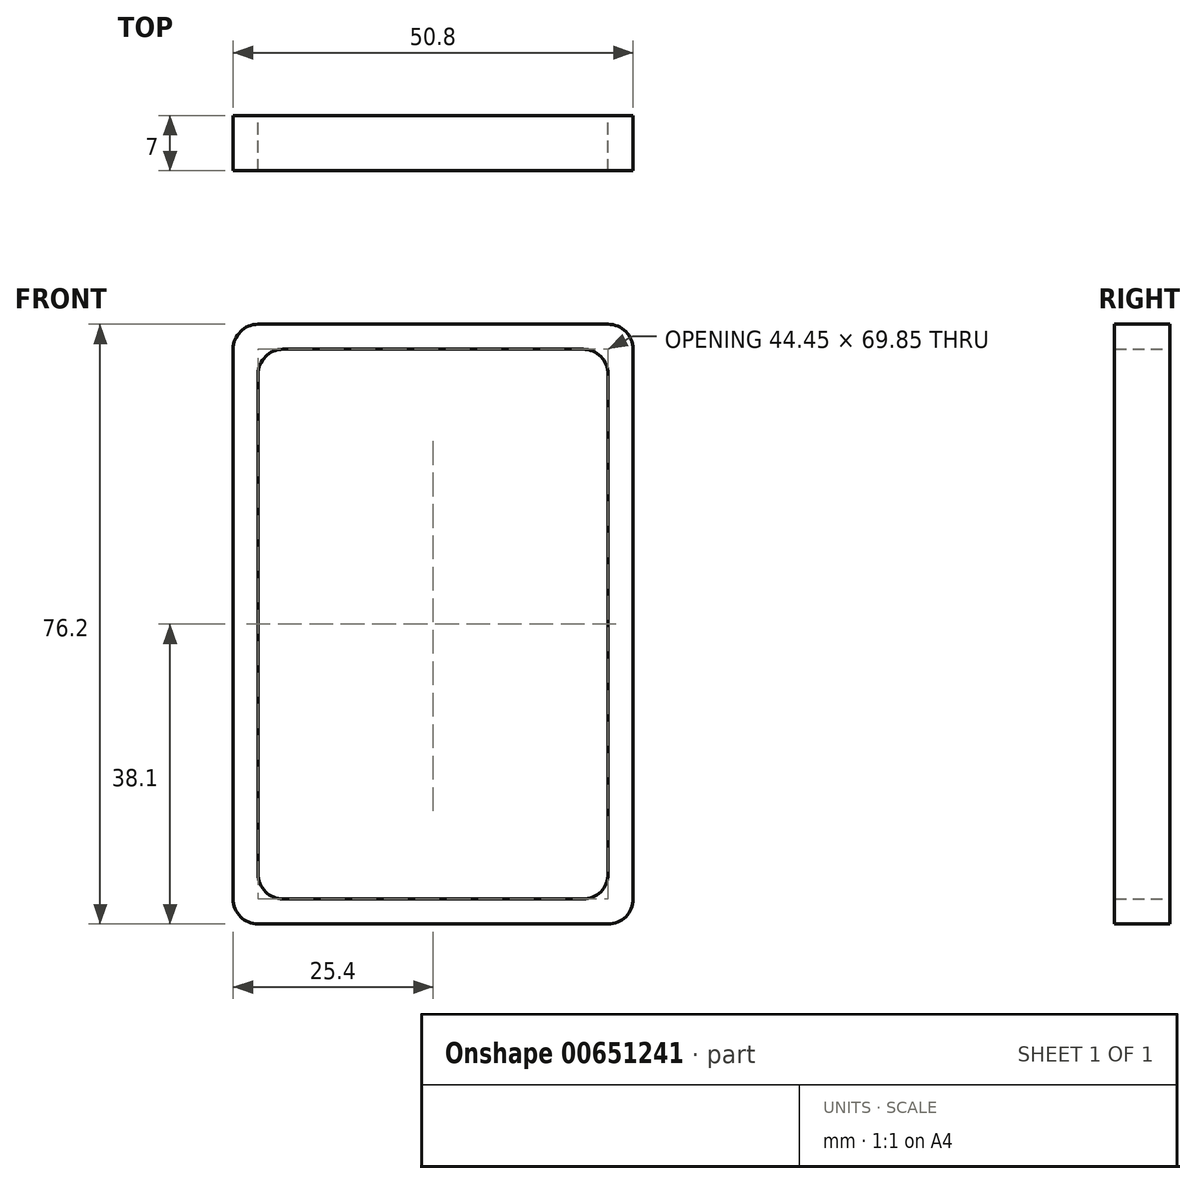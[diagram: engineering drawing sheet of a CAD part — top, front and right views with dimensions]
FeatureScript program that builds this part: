
annotation { "Feature Type Name" : "Feature", "Feature Type Description" : "" }
export const myFeature = defineFeature(function(context is Context, id is Id, definition is map)
    precondition{}
    {
        {
            var Q0;
            Q0=qCreatedBy(makeId("Front.planeOp"),FACE);
            var sketch = newSketch(context, id + "F0", { "sketchPlane" : qUnion([Q0])});
            skLineSegment(sketch, "E0.bottom", {"start": v(25.4, -38.1) * mm, "end": v(-25.4, -38.1) * mm});
            skLineSegment(sketch, "E0.top", {"start": v(25.4, 38.1) * mm, "end": v(-25.4, 38.1) * mm});
            skLineSegment(sketch, "E0.left", {"start": v(25.4, -38.1) * mm, "end": v(25.4, 38.1) * mm});
            skLineSegment(sketch, "E0.right", {"start": v(-25.4, -38.1) * mm, "end": v(-25.4, 38.1) * mm});
            skPoint(sketch, "E0.middle", {"position": v(0, 0) * mm});
            skLineSegment(sketch, "E1.bottom", {"start": v(22.22, -34.93) * mm, "end": v(-22.23, -34.93) * mm});
            skLineSegment(sketch, "E1.top", {"start": v(22.23, 34.93) * mm, "end": v(-22.23, 34.93) * mm});
            skLineSegment(sketch, "E1.left", {"start": v(22.22, -34.93) * mm, "end": v(22.23, 34.93) * mm});
            skLineSegment(sketch, "E1.right", {"start": v(-22.23, -34.93) * mm, "end": v(-22.23, 34.92) * mm});
            skSolve(sketch);
        }
        {
            assignVariable(context, id + "F1", {"name" : "Length", "anyValue" : 15 - 8});
        }
        {
            var Q0;
            Q0=makeQuery(id+"F0.imprint","IMPRINT",FACE,{"disambiguationData":[TD([[makeQuery(id+"F0.imprint","IMPRINT",EDGE,{"derivedFrom":sQuery(id+"F0.wireOp",EDGE,"E0.bottom")}),-1.0]])]});
            extrude(context, id + "F2", {"entities" : qUnion([Q0]), "depth" : (getVariable(context, 'Length')) * mm, "offsetDistance" : 25.4 * mm});
        }
        {
            var Q0;
            Q0=makeQuery(id+"F2.opExtrude","SWEPT_EDGE",EDGE,{"disambiguationData":[OSD([sQuery(id+"F0.wireOp",EDGE,"E1.top"),sQuery(id+"F0.wireOp",EDGE,"E1.right")])]});
            var Q1;
            Q1=makeQuery(id+"F2.opExtrude","SWEPT_EDGE",EDGE,{"disambiguationData":[OSD([sQuery(id+"F0.wireOp",EDGE,"E1.top"),sQuery(id+"F0.wireOp",EDGE,"E1.left")])]});
            var Q2;
            Q2=makeQuery(id+"F2.opExtrude","SWEPT_EDGE",EDGE,{"disambiguationData":[OSD([sQuery(id+"F0.wireOp",EDGE,"E1.bottom"),sQuery(id+"F0.wireOp",EDGE,"E1.left")])]});
            var Q3;
            Q3=makeQuery(id+"F2.opExtrude","SWEPT_EDGE",EDGE,{"disambiguationData":[OSD([sQuery(id+"F0.wireOp",EDGE,"E1.bottom"),sQuery(id+"F0.wireOp",EDGE,"E1.right")])]});
            var Q4;
            Q4=makeQuery(id+"F2.opExtrude","SWEPT_EDGE",EDGE,{"disambiguationData":[OSD([sQuery(id+"F0.wireOp",EDGE,"E0.top"),sQuery(id+"F0.wireOp",EDGE,"E0.left")])]});
            var Q5;
            Q5=makeQuery(id+"F2.opExtrude","SWEPT_EDGE",EDGE,{"disambiguationData":[OSD([sQuery(id+"F0.wireOp",EDGE,"E0.bottom"),sQuery(id+"F0.wireOp",EDGE,"E0.left")])]});
            var Q6;
            Q6=makeQuery(id+"F2.opExtrude","SWEPT_EDGE",EDGE,{"disambiguationData":[OSD([sQuery(id+"F0.wireOp",EDGE,"E0.top"),sQuery(id+"F0.wireOp",EDGE,"E0.right")])]});
            var Q7;
            Q7=makeQuery(id+"F2.opExtrude","SWEPT_EDGE",EDGE,{"disambiguationData":[OSD([sQuery(id+"F0.wireOp",EDGE,"E0.bottom"),sQuery(id+"F0.wireOp",EDGE,"E0.right")])]});
            fillet(context, id + "F3", {"entities" : qUnion([Q0, Q1, Q2, Q3, Q4, Q5, Q6, Q7]), "radius" : 3.17 * mm, "tangentPropagation" : true, "allowEdgeOverflow" : false});
        }
    });
